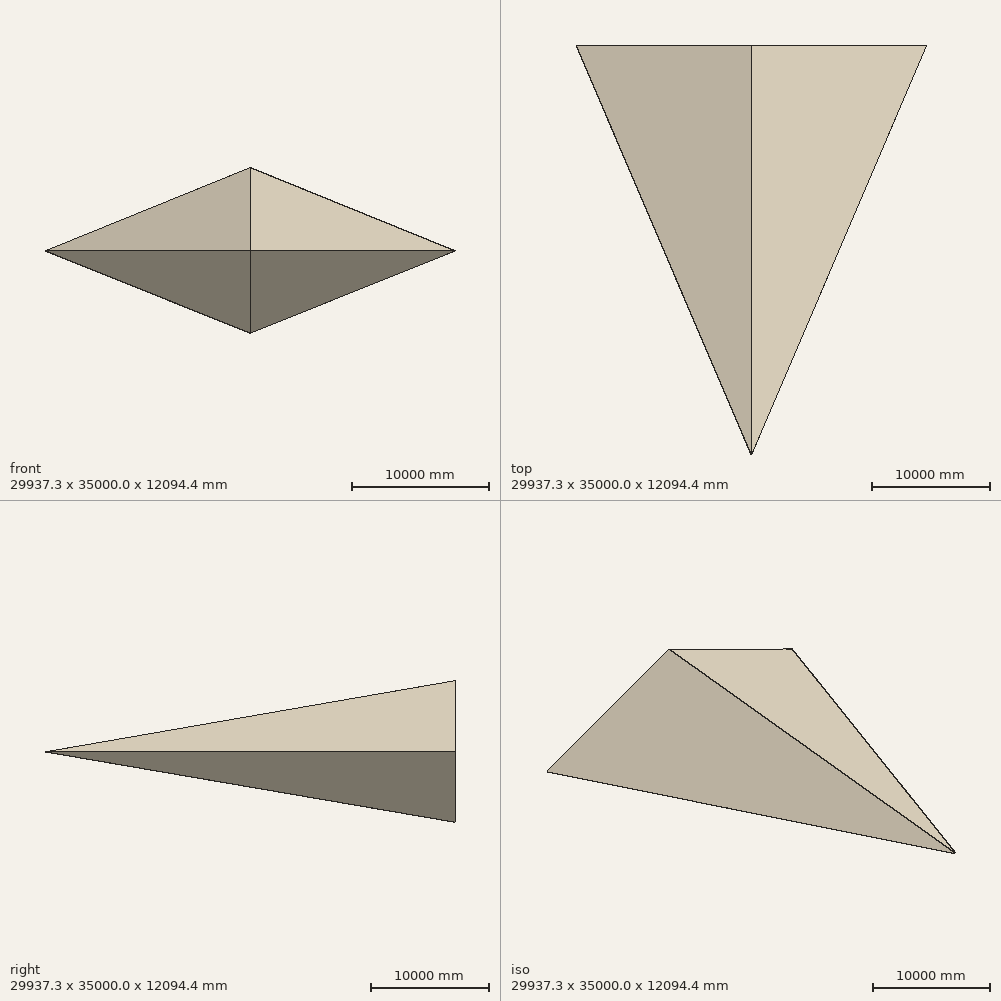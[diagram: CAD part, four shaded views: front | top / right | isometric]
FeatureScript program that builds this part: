
annotation { "Feature Type Name" : "Feature", "Feature Type Description" : "" }
export const myFeature = defineFeature(function(context is Context, id is Id, definition is map)
    precondition{}
    {
        {
            var Q0;
            Q0=qCreatedBy(makeId("Top.planeOp"),FACE);
            var sketch = newSketch(context, id + "F0", { "sketchPlane" : qUnion([Q0])});
            skLineSegment(sketch, "E0", {"start": v(0, 0) * mm, "end": v(0, -35000) * mm});
            skLineSegment(sketch, "E1", {"start": v(0, -35000) * mm, "end": v(0, -35000) * mm});
            skLineSegment(sketch, "E2", {"start": v(10488.63, -6527.58) * mm, "end": v(0, -35000) * mm});
            skLineSegment(sketch, "E3", {"start": v(10488.63, -6527.58) * mm, "end": v(15111.82, -3652.54) * mm});
            skLineSegment(sketch, "E4", {"start": v(15111.82, -3652.54) * mm, "end": v(11763.23, 0) * mm});
            skLineSegment(sketch, "E5", {"start": v(11763.23, 0) * mm, "end": v(11763.23, 0) * mm});
            skLineSegment(sketch, "E6", {"start": v(6076.22, 173.7) * mm, "end": v(11763.23, 0) * mm});
            skLineSegment(sketch, "E7", {"start": v(6076.22, 173.7) * mm, "end": v(0, 0) * mm});
            skSolve(sketch);
        }
        {
            var Q0;
            Q0=qCreatedBy(makeId("Front.planeOp"),FACE);
            var sketch = newSketch(context, id + "F1", { "sketchPlane" : qUnion([Q0])});
            skLineSegment(sketch, "E8", {"start": v(0, 0) * mm, "end": v(0, 6082.79) * mm});
            skLineSegment(sketch, "E9", {"start": v(0, 6082.79) * mm, "end": v(0, 6082.79) * mm});
            skLineSegment(sketch, "E10", {"start": v(14968.67, 0) * mm, "end": v(0, 6082.79) * mm});
            skLineSegment(sketch, "E11", {"start": v(0, -6011.58) * mm, "end": v(14968.67, 0) * mm});
            skLineSegment(sketch, "E12", {"start": v(0, -6011.58) * mm, "end": v(0, -6011.58) * mm});
            skLineSegment(sketch, "E13", {"start": v(-139.43, -1401.27) * mm, "end": v(0, 0) * mm});
            skLineSegment(sketch, "E14", {"start": v(0, -6011.58) * mm, "end": v(-139.43, -1401.27) * mm});
            skSolve(sketch);
        }
        {
            var Q0;
            Q0=sQuery(id+"F0.wireOp",VERTEX,"E0.end");
            var Q1;
            Q1=makeQuery(id+"F1.imprint","IMPRINT",FACE,{"disambiguationData":[TD([[makeQuery(id+"F1.imprint","IMPRINT",EDGE,{"derivedFrom":sQuery(id+"F1.wireOp",EDGE,"E8")}),-1.0]])]});
            loft(context, id + "F2", {"sheetProfilesArray" : [{ "sheetProfileEntities" : qUnion([Q0]) }, { "sheetProfileEntities" : qUnion([Q1]) }]});
        }
        {
            var Q0;
            Q0=makeQuery(id+"F2.opLoft","SWEPT_BODY",BODY,{"disambiguationData":[OSD([sQuery(id+"F0.wireOp",VERTEX,"E0.end"),makeQuery(id+"F1.imprint","IMPRINT",FACE,{"disambiguationData":[TD([[makeQuery(id+"F1.imprint","IMPRINT",EDGE,{"derivedFrom":sQuery(id+"F1.wireOp",EDGE,"E8")}),-1.0]])]})])]});
            var Q1;
            Q1=qCreatedBy(makeId("Right.planeOp"),FACE);
            mirror(context, id + "F3", {"operationType" : NewBodyOperationType.ADD, "entities" : qUnion([Q0]), "mirrorPlane" : qUnion([Q1])});
        }
    });
